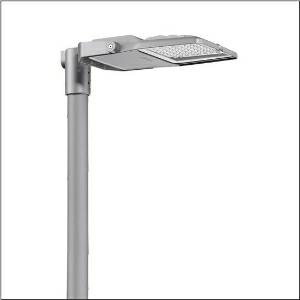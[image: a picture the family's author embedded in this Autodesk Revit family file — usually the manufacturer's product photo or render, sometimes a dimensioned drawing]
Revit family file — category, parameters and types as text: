
# Revit family: floodlight_fl_21_mini___pl52_5xa7772d2d3a_72a2
name_source: partatom
category: Lighting Fixtures
units: mm (PartAtom-declared; Revit-internal decimal feet)

## family parameters
Cut with Voids When Loaded = No
Host = Face
Light Source = No
Part Type = Normal
Room Calculation Point = No
Round Connector Dimension = Use Diameter
Shared = No

## types (1)
- --- (1 x LED, 17830 lm, 143 W, 3000K)
    Apparent Load = 143 VA
    CIE Flux Codes = 26 60 98 100 100
    Color Rendering = 70
    Color Temperature = 3000K
    Default Elevation = 1800 mm
    Description = Floodlight FL 21 mini, floodlight, primary light control with lens, of PMMA, primary optical cover: protective disc, of toughened safety glass, transparent, light distribution: PL52, light emission: direct distribution, installation type: surface-mounted, LED, High Power LED, rated luminous flux: 17.830lm, luminous efficacy: 125lm/W, light colour: 730, colour temperature: 3000K, control gear: ECG iQ, control: Auto-Match, Temp-Guard, Night-Set, Smart-Wire, Desk-Remote (wireless, voltage-free reading and setting of iQ features in the workshop via application-optimized NFC function/RFID function), optimised constant luminous flux control (CLO 2.0), Light-Fading, Lumen-Switch, with terminal, 6-pole, mains connection: 220..240V, AC, 50/60Hz, start of lifetime: 143W, end of lifetime: 152W, reduction: 61W, luminaire housing, of diecast aluminium, powder-coated, Siteco® metallic grey (DB 702S), corrosivity category C5 according to DIN EN ISO 12944, mast bracket, of steel, galvanised, powder-coated, protection rating (complete): IP66, insulation class (complete): insulation class II (safety insulation), certification: CE, ENEC, VDE, protection symbol: D, impact resistance: IK08, permissible operating ambient temperature: -40..+40°C, permissible operating ambient temperature for outdoor applications: -40..+50°C, standard: DIN EN 12944, packaging unit: 1 piece

Light Distribution: PL52
    Height = 70 mm
    Lamp = 1 x LED
    Lamp Light Flux = 17830 lm
    Lamp Power = 143 W
    Lamp count = 1
    Length = 485 mm
    Luminous efficacy = 125 lm/W
    Manufacturer = Siteco
    ModVariant = No
    Model = 5XA7772D2D3A
    Number of Poles = 1
    OnlyDefault = Yes
    Power Factor = 1
    Product Name = Floodlight FL 21 mini | PL52
    Product group = floodlight | pylon top
    ProductGroupID = 6101
    Protection Class = Protection class II
    Protection Degree = IP 66
    RLX_Detail_Level = 1
    RlxData = <blob elided: 101657 chars, md5=b651b466>
    Socket = socket
    Standby Power = 0 W
    System Light Flux = 17830 lm
    System Power = 143 W
    Type Comments = factory setting: luminous flux: 100 % | dim-lin: 254 | 730 mA
    Type Image = l_1007125.jpg
    URL = http://relux.com
    VarID = @adj_074831
    Voltage = 0 V
    Weight = 0.00 kg
    Width = 337 mm

## geometry (parser evidence)
native form markers: Blend x4, Sweep x12
no freeform markers — native parametric forms only
